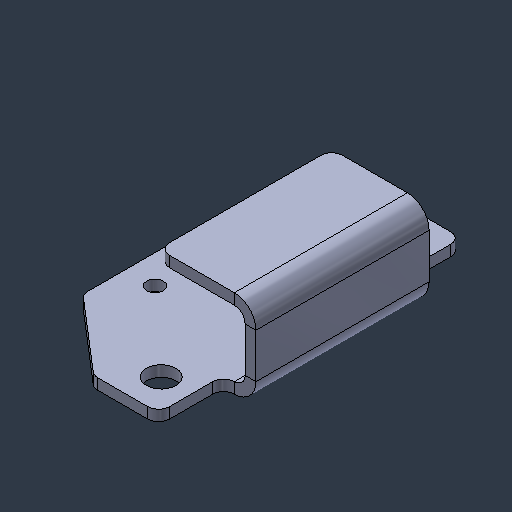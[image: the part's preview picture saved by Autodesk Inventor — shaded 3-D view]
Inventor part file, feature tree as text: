
AUTODESK INVENTOR PART (.ipt)
format: ipt  version: 2024.3 (Build 283343000, 343)  size: 117,248 bytes
history: native  units: mm (DEFAULTED — no unit token found)
features: fillet x1
ambient origin geometry x8: Origin, YZ Plane, XZ Plane, XY Plane, X Axis, Y Axis, Z Axis, Center Point
bodies: Solid1 (feature_tree)
feature tree (1):
  fillet  "Fillet1"  [1 undecoded]
note: 1 required parameter value undecoded (feature->parameter linkage not recoverable at this tier; creation-order binding heuristic only, values carry confidence <= 0.55)
